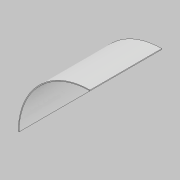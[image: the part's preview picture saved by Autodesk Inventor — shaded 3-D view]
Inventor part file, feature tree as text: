
AUTODESK INVENTOR PART (.ipt)
format: ipt  version: 2021 (Build 250183000, 183)  size: 93,184 bytes
history: native  units: mm
features: extrude x1, sketch x1
ambient origin geometry x8: Origin, YZ Plane, XZ Plane, XY Plane, X Axis, Y Axis, Z Axis, Center Point
bodies: Solid1 (feature_tree)
feature tree (2):
  extrude  "Extrusion1"  Depth=900.0mm
  sketch  "Sketch1"  dims[d0=10.0mm d1=900.0mm d2=0.0mm d3=0.0mm d4=900.0mm d5=0.0mm]
